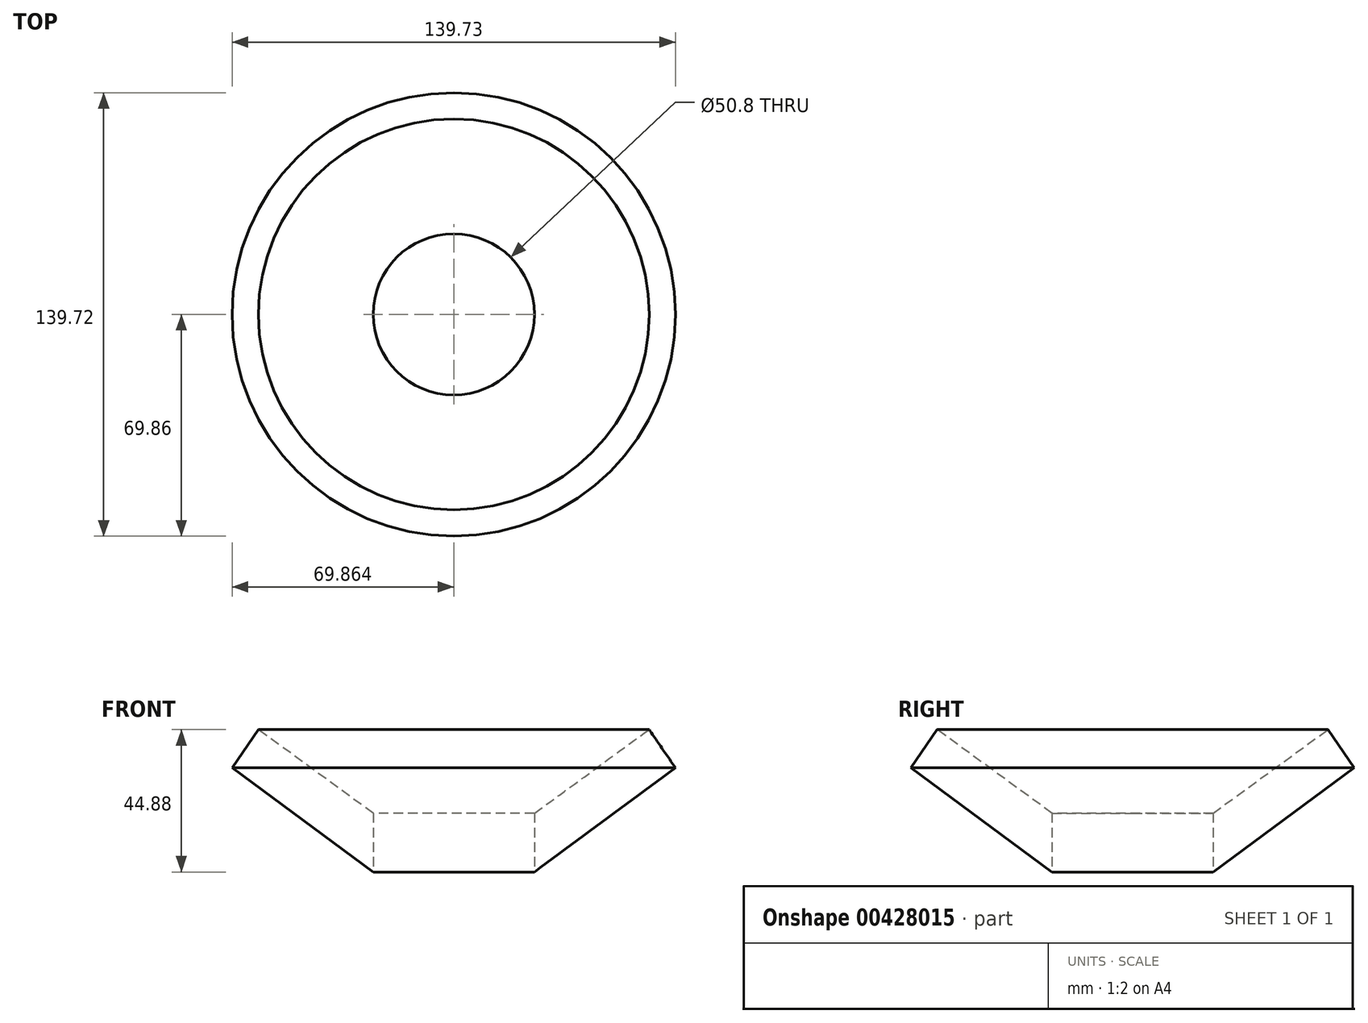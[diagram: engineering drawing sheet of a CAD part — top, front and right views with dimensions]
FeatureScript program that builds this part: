
annotation { "Feature Type Name" : "Feature", "Feature Type Description" : "" }
export const myFeature = defineFeature(function(context is Context, id is Id, definition is map)
    precondition{}
    {
        {
            var Q0;
            Q0=qCreatedBy(makeId("Front.planeOp"),FACE);
            var sketch = newSketch(context, id + "F0", { "sketchPlane" : qUnion([Q0])});
            skLineSegment(sketch, "E0.top", {"start": v(-58.13, -40.29) * mm, "end": v(-32.73, -40.29) * mm});
            skLineSegment(sketch, "E0.left", {"start": v(-58.13, -14.89) * mm, "end": v(-58.13, -40.29) * mm});
            skLineSegment(sketch, "E0.right", {"start": v(-32.73, -14.89) * mm, "end": v(-32.73, -40.29) * mm});
            skLineSegment(sketch, "E1", {"start": v(-58.13, -14.89) * mm, "end": v(3.45, 30) * mm});
            skLineSegment(sketch, "E2", {"start": v(-32.73, -14.89) * mm, "end": v(11.74, 17.94) * mm});
            skLineSegment(sketch, "E3", {"start": v(11.74, 17.94) * mm, "end": v(3.45, 30) * mm});
            skSolve(sketch);
        }
        {
            var Q0;
            Q0=makeQuery(id+"F0.imprint","IMPRINT",FACE,{"disambiguationData":[TD([[makeQuery(id+"F0.imprint","IMPRINT",EDGE,{"derivedFrom":sQuery(id+"F0.wireOp",EDGE,"E0.top")}),1.0]])]});
            var Q1;
            Q1=sQuery(id+"F0.wireOp",EDGE,"E0.left");
            revolve(context, id + "F1", {"entities" : qUnion([Q0]), "axis" : qUnion([Q1]), "revolveType" : RevolveType.FULL});
        }
        {
            var Q0;
            Q0=makeQuery(id+"F1.opRevolve","SWEPT_FACE",FACE,{"disambiguationData":[OSD([sQuery(id+"F0.wireOp",EDGE,"E0.top")])]});
            var sketch = newSketch(context, id + "F2", { "sketchPlane" : qUnion([Q0])});
            skCircle(sketch, "E4", {"center": v(-58.13, 0) * mm, "radius": 25.4 * mm});
            skSolve(sketch);
        }
        {
            var Q0;
            Q0=makeQuery(id+"F2.imprint","IMPRINT",FACE,{"disambiguationData":[TD([[makeQuery(id+"F2.imprint","IMPRINT",EDGE,{"derivedFrom":sQuery(id+"F2.wireOp",EDGE,"E4")}),-1.0]])]});
            extrude(context, id + "F3", {"entities" : qUnion([Q0]), "depth" : 25.4 * mm});
        }
        {
            var Q0;
            Q0=makeQuery(id+"F3.opExtrude","CAP_FACE",FACE,{"disambiguationData":[OSD([sQuery(id+"F2.wireOp",EDGE,"E4")])],"isStart":false});
            extrude(context, id + "F4", {"entities" : qUnion([Q0]), "operationType" : NewBodyOperationType.REMOVE, "oppositeDirection" : true, "depth" : 76.2 * mm});
        }
    });
